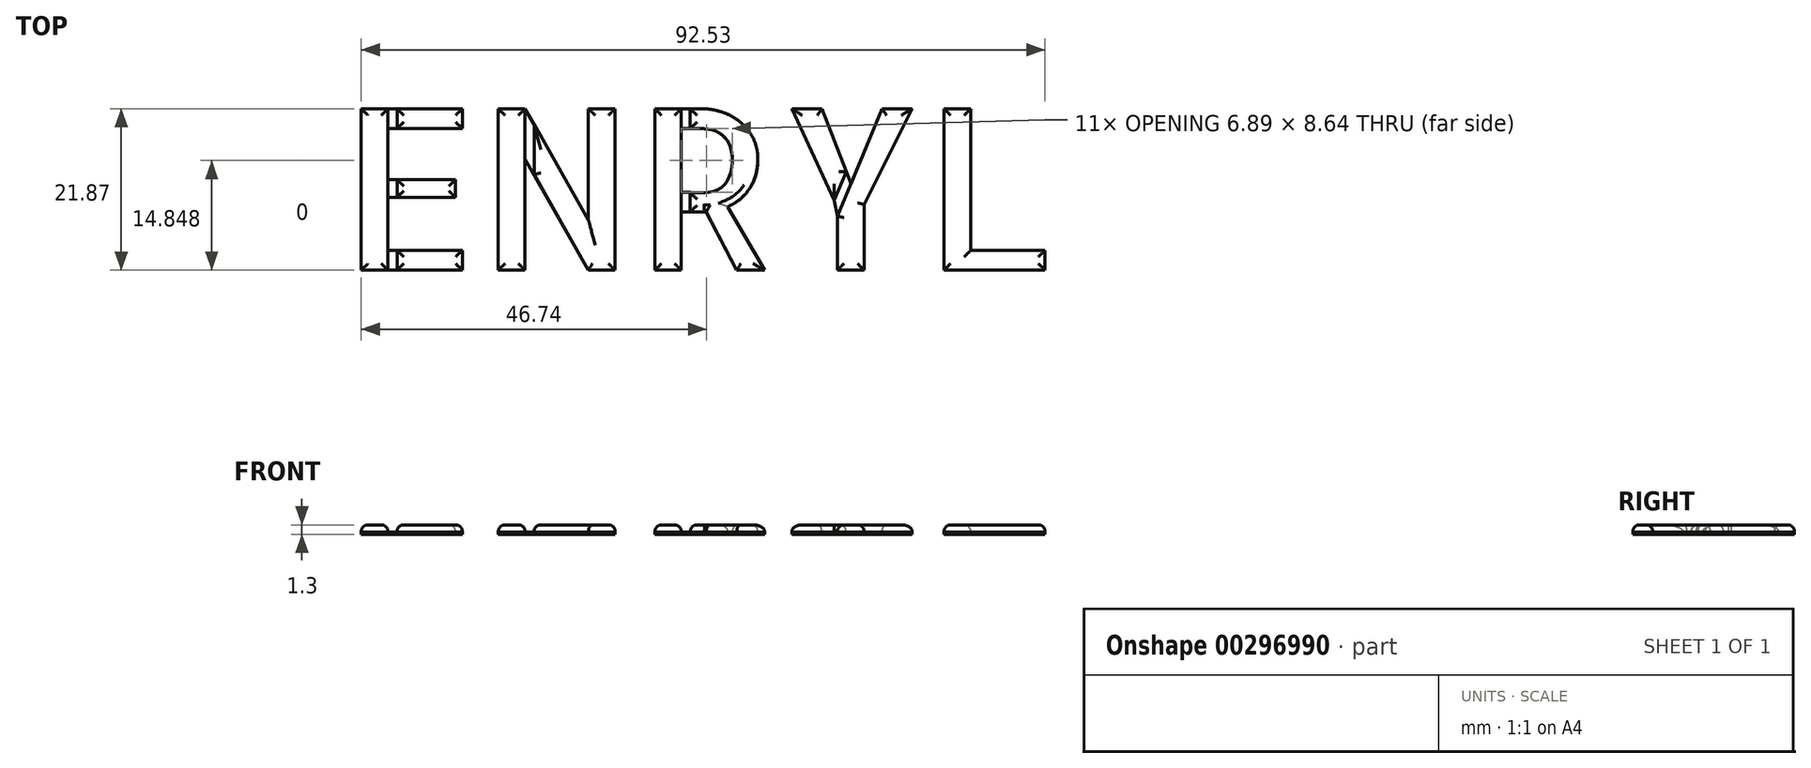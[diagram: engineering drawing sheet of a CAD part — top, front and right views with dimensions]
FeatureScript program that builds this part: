
annotation { "Feature Type Name" : "Feature", "Feature Type Description" : "" }
export const myFeature = defineFeature(function(context is Context, id is Id, definition is map)
    precondition{}
    {
        {
            var Q0;
            Q0=qCreatedBy(makeId("Top.planeOp"),FACE);
            var sketch = newSketch(context, id + "F0", { "sketchPlane" : qUnion([Q0])});
            skText(sketch, "E0", { "text": "ENRYL", "fontName": "AllertaStencil-Regular.ttf"});
            const initialGuessF0  = {"E0": [-0.04375, 0.01046, 1, 0, 0.02188]};
            skSetInitialGuess(sketch, initialGuessF0);
            skSolve(sketch);
        }
        {
            var Q0;
            Q0 = qSketchRegion(id + "F0", true);
            extrude(context, id + "F1", {"entities" : qUnion([Q0]), "depth" : 1 * mm, "offsetDistance" : 25 * mm});
        }
        {
            var Q0;
            Q0=makeQuery(id+"F1.opExtrude","CAP_FACE",FACE,{"disambiguationData":[OSD([sQuery(id+"F0.wireOp",EDGE,"E0.sketch_text.stroke-67"),sQuery(id+"F0.wireOp",EDGE,"E0.sketch_text.stroke-68"),sQuery(id+"F0.wireOp",EDGE,"E0.sketch_text.stroke-69"),sQuery(id+"F0.wireOp",EDGE,"E0.sketch_text.stroke-70"),sQuery(id+"F0.wireOp",EDGE,"E0.sketch_text.stroke-71"),sQuery(id+"F0.wireOp",EDGE,"E0.sketch_text.stroke-72")])],"isStart":false});
            var Q1;
            Q1=makeQuery(id+"F1.opExtrude","CAP_FACE",FACE,{"disambiguationData":[OSD([sQuery(id+"F0.wireOp",EDGE,"E0.sketch_text.stroke-57"),sQuery(id+"F0.wireOp",EDGE,"E0.sketch_text.stroke-58"),sQuery(id+"F0.wireOp",EDGE,"E0.sketch_text.stroke-59"),sQuery(id+"F0.wireOp",EDGE,"E0.sketch_text.stroke-60"),sQuery(id+"F0.wireOp",EDGE,"E0.sketch_text.stroke-61"),sQuery(id+"F0.wireOp",EDGE,"E0.sketch_text.stroke-62")])],"isStart":false});
            var Q2;
            Q2=makeQuery(id+"F1.opExtrude","CAP_FACE",FACE,{"disambiguationData":[OSD([sQuery(id+"F0.wireOp",EDGE,"E0.sketch_text.stroke-63"),sQuery(id+"F0.wireOp",EDGE,"E0.sketch_text.stroke-64"),sQuery(id+"F0.wireOp",EDGE,"E0.sketch_text.stroke-65"),sQuery(id+"F0.wireOp",EDGE,"E0.sketch_text.stroke-66")])],"isStart":false});
            var Q3;
            Q3=makeQuery(id+"F1.opExtrude","CAP_FACE",FACE,{"disambiguationData":[OSD([sQuery(id+"F0.wireOp",EDGE,"E0.sketch_text.stroke-31"),sQuery(id+"F0.wireOp",EDGE,"E0.sketch_text.stroke-32"),sQuery(id+"F0.wireOp",EDGE,"E0.sketch_text.stroke-33"),sQuery(id+"F0.wireOp",EDGE,"E0.sketch_text.stroke-34"),sQuery(id+"F0.wireOp",EDGE,"E0.sketch_text.stroke-35"),sQuery(id+"F0.wireOp",EDGE,"E0.sketch_text.stroke-36"),sQuery(id+"F0.wireOp",EDGE,"E0.sketch_text.stroke-37"),sQuery(id+"F0.wireOp",EDGE,"E0.sketch_text.stroke-38"),sQuery(id+"F0.wireOp",EDGE,"E0.sketch_text.stroke-39"),sQuery(id+"F0.wireOp",EDGE,"E0.sketch_text.stroke-40"),sQuery(id+"F0.wireOp",EDGE,"E0.sketch_text.stroke-41"),sQuery(id+"F0.wireOp",EDGE,"E0.sketch_text.stroke-42"),sQuery(id+"F0.wireOp",EDGE,"E0.sketch_text.stroke-43"),sQuery(id+"F0.wireOp",EDGE,"E0.sketch_text.stroke-44"),sQuery(id+"F0.wireOp",EDGE,"E0.sketch_text.stroke-45"),sQuery(id+"F0.wireOp",EDGE,"E0.sketch_text.stroke-46"),sQuery(id+"F0.wireOp",EDGE,"E0.sketch_text.stroke-47"),sQuery(id+"F0.wireOp",EDGE,"E0.sketch_text.stroke-48"),sQuery(id+"F0.wireOp",EDGE,"E0.sketch_text.stroke-49"),sQuery(id+"F0.wireOp",EDGE,"E0.sketch_text.stroke-50"),sQuery(id+"F0.wireOp",EDGE,"E0.sketch_text.stroke-51"),sQuery(id+"F0.wireOp",EDGE,"E0.sketch_text.stroke-52"),sQuery(id+"F0.wireOp",EDGE,"E0.sketch_text.stroke-53"),sQuery(id+"F0.wireOp",EDGE,"E0.sketch_text.stroke-54"),sQuery(id+"F0.wireOp",EDGE,"E0.sketch_text.stroke-55"),sQuery(id+"F0.wireOp",EDGE,"E0.sketch_text.stroke-56")])],"isStart":false});
            var Q4;
            Q4=makeQuery(id+"F1.opExtrude","CAP_FACE",FACE,{"disambiguationData":[OSD([sQuery(id+"F0.wireOp",EDGE,"E0.sketch_text.stroke-27"),sQuery(id+"F0.wireOp",EDGE,"E0.sketch_text.stroke-28"),sQuery(id+"F0.wireOp",EDGE,"E0.sketch_text.stroke-29"),sQuery(id+"F0.wireOp",EDGE,"E0.sketch_text.stroke-30")])],"isStart":false});
            var Q5;
            Q5=makeQuery(id+"F1.opExtrude","CAP_FACE",FACE,{"disambiguationData":[OSD([sQuery(id+"F0.wireOp",EDGE,"E0.sketch_text.stroke-16"),sQuery(id+"F0.wireOp",EDGE,"E0.sketch_text.stroke-17"),sQuery(id+"F0.wireOp",EDGE,"E0.sketch_text.stroke-18"),sQuery(id+"F0.wireOp",EDGE,"E0.sketch_text.stroke-19"),sQuery(id+"F0.wireOp",EDGE,"E0.sketch_text.stroke-20"),sQuery(id+"F0.wireOp",EDGE,"E0.sketch_text.stroke-21"),sQuery(id+"F0.wireOp",EDGE,"E0.sketch_text.stroke-22")])],"isStart":false});
            var Q6;
            Q6=makeQuery(id+"F1.opExtrude","CAP_FACE",FACE,{"disambiguationData":[OSD([sQuery(id+"F0.wireOp",EDGE,"E0.sketch_text.stroke-23"),sQuery(id+"F0.wireOp",EDGE,"E0.sketch_text.stroke-24"),sQuery(id+"F0.wireOp",EDGE,"E0.sketch_text.stroke-25"),sQuery(id+"F0.wireOp",EDGE,"E0.sketch_text.stroke-26")])],"isStart":false});
            var Q7;
            Q7=makeQuery(id+"F1.opExtrude","CAP_FACE",FACE,{"disambiguationData":[OSD([sQuery(id+"F0.wireOp",EDGE,"E0.sketch_text.stroke-0"),sQuery(id+"F0.wireOp",EDGE,"E0.sketch_text.stroke-1"),sQuery(id+"F0.wireOp",EDGE,"E0.sketch_text.stroke-2"),sQuery(id+"F0.wireOp",EDGE,"E0.sketch_text.stroke-3")])],"isStart":false});
            var Q8;
            Q8=makeQuery(id+"F1.opExtrude","CAP_FACE",FACE,{"disambiguationData":[OSD([sQuery(id+"F0.wireOp",EDGE,"E0.sketch_text.stroke-12"),sQuery(id+"F0.wireOp",EDGE,"E0.sketch_text.stroke-13"),sQuery(id+"F0.wireOp",EDGE,"E0.sketch_text.stroke-14"),sQuery(id+"F0.wireOp",EDGE,"E0.sketch_text.stroke-15")])],"isStart":false});
            var Q9;
            Q9=makeQuery(id+"F1.opExtrude","CAP_FACE",FACE,{"disambiguationData":[OSD([sQuery(id+"F0.wireOp",EDGE,"E0.sketch_text.stroke-4"),sQuery(id+"F0.wireOp",EDGE,"E0.sketch_text.stroke-5"),sQuery(id+"F0.wireOp",EDGE,"E0.sketch_text.stroke-6"),sQuery(id+"F0.wireOp",EDGE,"E0.sketch_text.stroke-7")])],"isStart":false});
            var Q10;
            Q10=makeQuery(id+"F1.opExtrude","CAP_FACE",FACE,{"disambiguationData":[OSD([sQuery(id+"F0.wireOp",EDGE,"E0.sketch_text.stroke-8"),sQuery(id+"F0.wireOp",EDGE,"E0.sketch_text.stroke-9"),sQuery(id+"F0.wireOp",EDGE,"E0.sketch_text.stroke-10"),sQuery(id+"F0.wireOp",EDGE,"E0.sketch_text.stroke-11")])],"isStart":false});
            var Q11;
            Q11=makeQuery(id+"F1.opExtrude","CAP_FACE",FACE,{"disambiguationData":[OSD([sQuery(id+"F0.wireOp",EDGE,"16d9248e-6218-4f41-ae3f-aeb82b8c0249.sketch_text.stroke-0"),sQuery(id+"F0.wireOp",EDGE,"16d9248e-6218-4f41-ae3f-aeb82b8c0249.sketch_text.stroke-1"),sQuery(id+"F0.wireOp",EDGE,"16d9248e-6218-4f41-ae3f-aeb82b8c0249.sketch_text.stroke-2"),sQuery(id+"F0.wireOp",EDGE,"16d9248e-6218-4f41-ae3f-aeb82b8c0249.sketch_text.stroke-3"),sQuery(id+"F0.wireOp",EDGE,"16d9248e-6218-4f41-ae3f-aeb82b8c0249.sketch_text.stroke-4"),sQuery(id+"F0.wireOp",EDGE,"16d9248e-6218-4f41-ae3f-aeb82b8c0249.sketch_text.stroke-5"),sQuery(id+"F0.wireOp",EDGE,"16d9248e-6218-4f41-ae3f-aeb82b8c0249.sketch_text.stroke-6"),sQuery(id+"F0.wireOp",EDGE,"16d9248e-6218-4f41-ae3f-aeb82b8c0249.sketch_text.stroke-7"),sQuery(id+"F0.wireOp",EDGE,"16d9248e-6218-4f41-ae3f-aeb82b8c0249.sketch_text.stroke-8"),sQuery(id+"F0.wireOp",EDGE,"16d9248e-6218-4f41-ae3f-aeb82b8c0249.sketch_text.stroke-9"),sQuery(id+"F0.wireOp",EDGE,"16d9248e-6218-4f41-ae3f-aeb82b8c0249.sketch_text.stroke-10"),sQuery(id+"F0.wireOp",EDGE,"16d9248e-6218-4f41-ae3f-aeb82b8c0249.sketch_text.stroke-11")])],"isStart":false});
            var Q12;
            Q12=makeQuery(id+"F1.opExtrude","CAP_FACE",FACE,{"disambiguationData":[OSD([sQuery(id+"F0.wireOp",EDGE,"16d9248e-6218-4f41-ae3f-aeb82b8c0249.sketch_text.stroke-12"),sQuery(id+"F0.wireOp",EDGE,"16d9248e-6218-4f41-ae3f-aeb82b8c0249.sketch_text.stroke-13"),sQuery(id+"F0.wireOp",EDGE,"16d9248e-6218-4f41-ae3f-aeb82b8c0249.sketch_text.stroke-14"),sQuery(id+"F0.wireOp",EDGE,"16d9248e-6218-4f41-ae3f-aeb82b8c0249.sketch_text.stroke-15"),sQuery(id+"F0.wireOp",EDGE,"16d9248e-6218-4f41-ae3f-aeb82b8c0249.sketch_text.stroke-16"),sQuery(id+"F0.wireOp",EDGE,"16d9248e-6218-4f41-ae3f-aeb82b8c0249.sketch_text.stroke-17"),sQuery(id+"F0.wireOp",EDGE,"16d9248e-6218-4f41-ae3f-aeb82b8c0249.sketch_text.stroke-18"),sQuery(id+"F0.wireOp",EDGE,"16d9248e-6218-4f41-ae3f-aeb82b8c0249.sketch_text.stroke-19"),sQuery(id+"F0.wireOp",EDGE,"16d9248e-6218-4f41-ae3f-aeb82b8c0249.sketch_text.stroke-20"),sQuery(id+"F0.wireOp",EDGE,"16d9248e-6218-4f41-ae3f-aeb82b8c0249.sketch_text.stroke-21"),sQuery(id+"F0.wireOp",EDGE,"16d9248e-6218-4f41-ae3f-aeb82b8c0249.sketch_text.stroke-22"),sQuery(id+"F0.wireOp",EDGE,"16d9248e-6218-4f41-ae3f-aeb82b8c0249.sketch_text.stroke-23"),sQuery(id+"F0.wireOp",EDGE,"16d9248e-6218-4f41-ae3f-aeb82b8c0249.sketch_text.stroke-24")])],"isStart":false});
            var Q13;
            Q13=makeQuery(id+"F1.opExtrude","CAP_FACE",FACE,{"disambiguationData":[OSD([sQuery(id+"F0.wireOp",EDGE,"16d9248e-6218-4f41-ae3f-aeb82b8c0249.sketch_text.stroke-25"),sQuery(id+"F0.wireOp",EDGE,"16d9248e-6218-4f41-ae3f-aeb82b8c0249.sketch_text.stroke-26"),sQuery(id+"F0.wireOp",EDGE,"16d9248e-6218-4f41-ae3f-aeb82b8c0249.sketch_text.stroke-27"),sQuery(id+"F0.wireOp",EDGE,"16d9248e-6218-4f41-ae3f-aeb82b8c0249.sketch_text.stroke-28"),sQuery(id+"F0.wireOp",EDGE,"16d9248e-6218-4f41-ae3f-aeb82b8c0249.sketch_text.stroke-29"),sQuery(id+"F0.wireOp",EDGE,"16d9248e-6218-4f41-ae3f-aeb82b8c0249.sketch_text.stroke-30"),sQuery(id+"F0.wireOp",EDGE,"16d9248e-6218-4f41-ae3f-aeb82b8c0249.sketch_text.stroke-31"),sQuery(id+"F0.wireOp",EDGE,"16d9248e-6218-4f41-ae3f-aeb82b8c0249.sketch_text.stroke-32"),sQuery(id+"F0.wireOp",EDGE,"16d9248e-6218-4f41-ae3f-aeb82b8c0249.sketch_text.stroke-33"),sQuery(id+"F0.wireOp",EDGE,"16d9248e-6218-4f41-ae3f-aeb82b8c0249.sketch_text.stroke-34"),sQuery(id+"F0.wireOp",EDGE,"16d9248e-6218-4f41-ae3f-aeb82b8c0249.sketch_text.stroke-35"),sQuery(id+"F0.wireOp",EDGE,"16d9248e-6218-4f41-ae3f-aeb82b8c0249.sketch_text.stroke-36"),sQuery(id+"F0.wireOp",EDGE,"16d9248e-6218-4f41-ae3f-aeb82b8c0249.sketch_text.stroke-37"),sQuery(id+"F0.wireOp",EDGE,"16d9248e-6218-4f41-ae3f-aeb82b8c0249.sketch_text.stroke-38"),sQuery(id+"F0.wireOp",EDGE,"16d9248e-6218-4f41-ae3f-aeb82b8c0249.sketch_text.stroke-39"),sQuery(id+"F0.wireOp",EDGE,"16d9248e-6218-4f41-ae3f-aeb82b8c0249.sketch_text.stroke-40"),sQuery(id+"F0.wireOp",EDGE,"16d9248e-6218-4f41-ae3f-aeb82b8c0249.sketch_text.stroke-41"),sQuery(id+"F0.wireOp",EDGE,"16d9248e-6218-4f41-ae3f-aeb82b8c0249.sketch_text.stroke-42"),sQuery(id+"F0.wireOp",EDGE,"16d9248e-6218-4f41-ae3f-aeb82b8c0249.sketch_text.stroke-43")])],"isStart":false});
            var Q14;
            Q14=makeQuery(id+"F1.opExtrude","CAP_FACE",FACE,{"disambiguationData":[OSD([sQuery(id+"F0.wireOp",EDGE,"16d9248e-6218-4f41-ae3f-aeb82b8c0249.sketch_text.stroke-44"),sQuery(id+"F0.wireOp",EDGE,"16d9248e-6218-4f41-ae3f-aeb82b8c0249.sketch_text.stroke-45"),sQuery(id+"F0.wireOp",EDGE,"16d9248e-6218-4f41-ae3f-aeb82b8c0249.sketch_text.stroke-46"),sQuery(id+"F0.wireOp",EDGE,"16d9248e-6218-4f41-ae3f-aeb82b8c0249.sketch_text.stroke-47"),sQuery(id+"F0.wireOp",EDGE,"16d9248e-6218-4f41-ae3f-aeb82b8c0249.sketch_text.stroke-48"),sQuery(id+"F0.wireOp",EDGE,"16d9248e-6218-4f41-ae3f-aeb82b8c0249.sketch_text.stroke-49"),sQuery(id+"F0.wireOp",EDGE,"16d9248e-6218-4f41-ae3f-aeb82b8c0249.sketch_text.stroke-50"),sQuery(id+"F0.wireOp",EDGE,"16d9248e-6218-4f41-ae3f-aeb82b8c0249.sketch_text.stroke-51"),sQuery(id+"F0.wireOp",EDGE,"16d9248e-6218-4f41-ae3f-aeb82b8c0249.sketch_text.stroke-52")])],"isStart":false});
            var Q15;
            Q15=makeQuery(id+"F1.opExtrude","CAP_FACE",FACE,{"disambiguationData":[OSD([sQuery(id+"F0.wireOp",EDGE,"16d9248e-6218-4f41-ae3f-aeb82b8c0249.sketch_text.stroke-53"),sQuery(id+"F0.wireOp",EDGE,"16d9248e-6218-4f41-ae3f-aeb82b8c0249.sketch_text.stroke-54"),sQuery(id+"F0.wireOp",EDGE,"16d9248e-6218-4f41-ae3f-aeb82b8c0249.sketch_text.stroke-55"),sQuery(id+"F0.wireOp",EDGE,"16d9248e-6218-4f41-ae3f-aeb82b8c0249.sketch_text.stroke-56"),sQuery(id+"F0.wireOp",EDGE,"16d9248e-6218-4f41-ae3f-aeb82b8c0249.sketch_text.stroke-57"),sQuery(id+"F0.wireOp",EDGE,"16d9248e-6218-4f41-ae3f-aeb82b8c0249.sketch_text.stroke-58")])],"isStart":false});
            fillet(context, id + "F2", {"entities" : qUnion([Q0, Q1, Q2, Q3, Q4, Q5, Q6, Q7, Q8, Q9, Q10, Q11, Q12, Q13, Q14, Q15]), "radius" : 0.9 * mm, "tangentPropagation" : true, "allowEdgeOverflow" : false});
        }
        {
            var Q0;
            Q0=qCreatedBy(makeId("Top.planeOp"),FACE);
            var sketch = newSketch(context, id + "F3", { "sketchPlane" : qUnion([Q0])});
            skLineSegment(sketch, "E1.bottom", {"start": v(-40.93, 10.46) * mm, "end": v(51.58, 10.46) * mm});
            skLineSegment(sketch, "E1.top", {"start": v(-40.93, 32.33) * mm, "end": v(51.58, 32.33) * mm});
            skLineSegment(sketch, "E1.left", {"start": v(-40.93, 10.46) * mm, "end": v(-40.93, 32.33) * mm});
            skLineSegment(sketch, "E1.right", {"start": v(51.58, 10.46) * mm, "end": v(51.58, 32.33) * mm});
            skSolve(sketch);
        }
        {
            var Q0;
            Q0 = qSketchRegion(id + "F3", true);
            extrude(context, id + "F4", {"entities" : qUnion([Q0]), "oppositeDirection" : true, "depth" : 0.3 * mm, "offsetDistance" : 25 * mm});
        }
        {
            var Q0;
            Q0=makeQuery(id+"F4.opExtrude","CAP_FACE",FACE,{"disambiguationData":[OSD([sQuery(id+"F3.wireOp",EDGE,"E1.bottom"),sQuery(id+"F3.wireOp",EDGE,"E1.top"),sQuery(id+"F3.wireOp",EDGE,"E1.left"),sQuery(id+"F3.wireOp",EDGE,"E1.right")])],"isStart":true});
            var sketch = newSketch(context, id + "F5", { "sketchPlane" : qUnion([Q0])});
            skLineSegment(sketch, "E2.bottom", {"start": v(-27.25, 29.63) * mm, "end": v(-37.31, 29.63) * mm});
            skLineSegment(sketch, "E2.top", {"start": v(-27.25, 22.75) * mm, "end": v(-37.31, 22.75) * mm});
            skLineSegment(sketch, "E2.left", {"start": v(-27.25, 29.63) * mm, "end": v(-27.25, 22.75) * mm});
            skLineSegment(sketch, "E2.right", {"start": v(-37.31, 29.63) * mm, "end": v(-37.31, 22.75) * mm});
            skLineSegment(sketch, "E3.bottom", {"start": v(-27.25, 22.75) * mm, "end": v(-28.17, 22.75) * mm});
            skLineSegment(sketch, "E3.top", {"start": v(-27.25, 20.31) * mm, "end": v(-28.17, 20.31) * mm});
            skLineSegment(sketch, "E3.left", {"start": v(-27.25, 22.75) * mm, "end": v(-27.25, 20.31) * mm});
            skLineSegment(sketch, "E3.right", {"start": v(-28.17, 22.75) * mm, "end": v(-28.17, 20.31) * mm});
            skLineSegment(sketch, "E4.bottom", {"start": v(-27.25, 20.31) * mm, "end": v(-37.31, 20.31) * mm});
            skLineSegment(sketch, "E4.top", {"start": v(-27.25, 13.16) * mm, "end": v(-37.31, 13.16) * mm});
            skLineSegment(sketch, "E4.left", {"start": v(-27.25, 20.31) * mm, "end": v(-27.25, 13.16) * mm});
            skLineSegment(sketch, "E4.right", {"start": v(-37.31, 20.31) * mm, "end": v(-37.31, 13.16) * mm});
            skLineSegment(sketch, "E5.bottom", {"start": v(-27.25, 32.33) * mm, "end": v(-22.39, 32.33) * mm});
            skLineSegment(sketch, "E5.top", {"start": v(-27.25, 10.46) * mm, "end": v(-22.39, 10.46) * mm});
            skLineSegment(sketch, "E5.left", {"start": v(-27.25, 32.33) * mm, "end": v(-27.25, 10.46) * mm});
            skLineSegment(sketch, "E5.right", {"start": v(-22.39, 32.33) * mm, "end": v(-22.39, 10.46) * mm});
            skLineSegment(sketch, "E6", {"start": v(-10.2, 10.46) * mm, "end": v(-18.77, 25.53) * mm});
            skLineSegment(sketch, "E7", {"start": v(-10.2, 10.46) * mm, "end": v(-18.77, 10.46) * mm});
            skLineSegment(sketch, "E8", {"start": v(-18.77, 25.53) * mm, "end": v(-18.77, 10.46) * mm});
            skLineSegment(sketch, "E9", {"start": v(-18.77, 32.33) * mm, "end": v(-10.2, 17.26) * mm});
            skLineSegment(sketch, "E10", {"start": v(-10.2, 17.26) * mm, "end": v(-10.2, 32.33) * mm});
            skLineSegment(sketch, "E11", {"start": v(-10.2, 32.33) * mm, "end": v(-18.77, 32.33) * mm});
            skLineSegment(sketch, "E12.bottom", {"start": v(-6.57, 32.33) * mm, "end": v(-1.2, 32.33) * mm});
            skLineSegment(sketch, "E12.top", {"start": v(-6.57, 10.46) * mm, "end": v(-1.2, 10.46) * mm});
            skLineSegment(sketch, "E12.left", {"start": v(-6.57, 32.33) * mm, "end": v(-6.57, 10.46) * mm});
            skLineSegment(sketch, "E12.right", {"start": v(-1.2, 32.33) * mm, "end": v(-1.2, 10.46) * mm});
            skLineSegment(sketch, "E13.bottom", {"start": v(5.73, 18.35) * mm, "end": v(2.36, 18.35) * mm});
            skLineSegment(sketch, "E13.top", {"start": v(5.73, 10.46) * mm, "end": v(2.36, 10.46) * mm});
            skLineSegment(sketch, "E13.left", {"start": v(5.73, 18.35) * mm, "end": v(5.73, 10.46) * mm});
            skLineSegment(sketch, "E13.right", {"start": v(2.36, 18.35) * mm, "end": v(2.36, 10.46) * mm});
            skLineSegment(sketch, "E14", {"start": v(5.73, 10.46) * mm, "end": v(9.86, 10.46) * mm});
            skLineSegment(sketch, "E15", {"start": v(9.86, 10.46) * mm, "end": v(5.73, 18.35) * mm});
            skArc(sketch, "E16", {"start": v(3.62, 20.99) * mm, "mid": v(7.95, 25.34) * mm, "end": v(3.56, 29.63) * mm});
            skFitSpline(sketch, "E17", {"points": [v(3.56, 29.63) * mm, v(5.23, 29.63) * mm, v(5.87, 29.58) * mm, v(6.33, 29.51) * mm, v(6.75, 29.4) * mm, v(7.1, 29.26) * mm, v(7.44, 29.08) * mm, v(7.84, 28.81) * mm, v(8.18, 28.52) * mm, v(8.5, 28.16) * mm, v(8.74, 27.8) * mm, v(8.82, 27.65) * mm, v(8.92, 27.44) * mm, v(9.04, 27.11) * mm, v(9.12, 26.78) * mm, v(9.2, 26.4) * mm, v(9.25, 25.97) * mm, v(9.27, 25.53) * mm, v(9.25, 25.03) * mm, v(9.22, 24.54) * mm, v(9.13, 24) * mm, v(9.03, 23.58) * mm, v(8.9, 23.2) * mm, v(8.7, 22.77) * mm, v(8.54, 22.48) * mm, v(8.36, 22.22) * mm, v(8.1, 21.94) * mm, v(7.84, 21.7) * mm, v(7.5, 21.48) * mm, v(7.2, 21.31) * mm, v(6.9, 21.2) * mm, v(6.61, 21.1) * mm, v(6.16, 21.01) * mm, v(5.8, 20.98) * mm, v(5.28, 20.97) * mm, v(4.65, 20.98) * mm, v(3.62, 20.99) * mm], "startDerivative": vector(34.61, 0.36) * mm, "endDerivative": vector(-25.88, 0.32) * mm});
            skLineSegment(sketch, "E18.bottom", {"start": v(3.56, 29.63) * mm, "end": v(2.36, 29.63) * mm});
            skLineSegment(sketch, "E18.top", {"start": v(3.56, 20.99) * mm, "end": v(2.36, 20.99) * mm});
            skLineSegment(sketch, "E18.left", {"start": v(3.56, 29.63) * mm, "end": v(3.56, 20.99) * mm});
            skLineSegment(sketch, "E18.right", {"start": v(2.36, 29.63) * mm, "end": v(2.36, 20.99) * mm});
            skLineSegment(sketch, "E19", {"start": v(3.62, 20.99) * mm, "end": v(3.56, 20.99) * mm});
            skFitSpline(sketch, "E20", {"points": [v(5.1, 32.33) * mm, v(5.45, 32.33) * mm, v(5.92, 32.3) * mm, v(6.44, 32.22) * mm, v(7, 32.13) * mm, v(7.6, 31.97) * mm, v(7.83, 31.9) * mm, v(8.24, 31.75) * mm, v(8.6, 31.6) * mm, v(9, 31.4) * mm, v(9.43, 31.17) * mm, v(9.82, 30.91) * mm, v(10.19, 30.64) * mm, v(10.62, 30.27) * mm, v(11.06, 29.83) * mm, v(11.36, 29.48) * mm, v(11.66, 29.05) * mm, v(11.96, 28.58) * mm, v(12.15, 28.2) * mm, v(12.3, 27.84) * mm, v(12.44, 27.48) * mm, v(12.55, 27.04) * mm, v(12.65, 26.56) * mm, v(12.7, 26.18) * mm, v(12.72, 25.82) * mm, v(12.72, 25.46) * mm, v(12.7, 25.07) * mm, v(12.68, 24.67) * mm, v(12.62, 24.17) * mm, v(12.48, 23.49) * mm, v(12.33, 22.97) * mm, v(12.15, 22.51) * mm, v(11.94, 22.07) * mm, v(11.73, 21.7) * mm, v(11.57, 21.45) * mm, v(11.36, 21.17) * mm, v(11.1, 20.84) * mm, v(10.84, 20.56) * mm, v(10.62, 20.35) * mm, v(10.37, 20.12) * mm, v(10.08, 19.9) * mm, v(9.75, 19.66) * mm, v(9.4, 19.44) * mm, v(9.12, 19.3) * mm, v(8.88, 19.18) * mm, v(8.66, 19.07) * mm], "startDerivative": vector(17.18, 0.3) * mm, "endDerivative": vector(-13.02, -6.11) * mm});
            skLineSegment(sketch, "E21", {"start": v(8.66, 19.07) * mm, "end": v(13.63, 10.46) * mm});
            skLineSegment(sketch, "E22", {"start": v(13.63, 10.46) * mm, "end": v(23.48, 10.46) * mm});
            skLineSegment(sketch, "E23", {"start": v(23.48, 10.46) * mm, "end": v(23.48, 17.76) * mm});
            skLineSegment(sketch, "E24", {"start": v(23.48, 17.76) * mm, "end": v(23.07, 19.93) * mm});
            skLineSegment(sketch, "E25", {"start": v(23.07, 19.93) * mm, "end": v(17.31, 32.33) * mm});
            skLineSegment(sketch, "E26", {"start": v(17.31, 32.33) * mm, "end": v(5.1, 32.33) * mm});
            skLineSegment(sketch, "E27", {"start": v(21.38, 32.33) * mm, "end": v(25.31, 22.17) * mm});
            skLineSegment(sketch, "E28", {"start": v(25.31, 22.17) * mm, "end": v(29.54, 32.33) * mm});
            skLineSegment(sketch, "E29", {"start": v(29.54, 32.33) * mm, "end": v(21.38, 32.33) * mm});
            skLineSegment(sketch, "E30", {"start": v(33.6, 32.33) * mm, "end": v(27.1, 19.36) * mm});
            skLineSegment(sketch, "E31", {"start": v(27.1, 19.36) * mm, "end": v(27.1, 10.46) * mm});
            skLineSegment(sketch, "E32", {"start": v(27.1, 10.46) * mm, "end": v(37.9, 10.46) * mm});
            skLineSegment(sketch, "E33", {"start": v(37.9, 32.33) * mm, "end": v(33.6, 32.33) * mm});
            skLineSegment(sketch, "E34", {"start": v(37.9, 32.33) * mm, "end": v(37.9, 10.46) * mm});
            skLineSegment(sketch, "E35.bottom", {"start": v(41.52, 32.33) * mm, "end": v(51.58, 32.33) * mm});
            skLineSegment(sketch, "E35.top", {"start": v(41.52, 13.16) * mm, "end": v(51.58, 13.16) * mm});
            skLineSegment(sketch, "E35.left", {"start": v(41.52, 32.33) * mm, "end": v(41.52, 13.16) * mm});
            skLineSegment(sketch, "E35.right", {"start": v(51.58, 32.33) * mm, "end": v(51.58, 13.16) * mm});
            skSolve(sketch);
        }
        {
            var Q0;
            Q0 = qSketchRegion(id + "F5", true);
            extrude(context, id + "F6", {"entities" : qUnion([Q0]), "operationType" : NewBodyOperationType.REMOVE, "oppositeDirection" : true, "depth" : 0.3 * mm, "offsetDistance" : 25 * mm});
        }
    });
